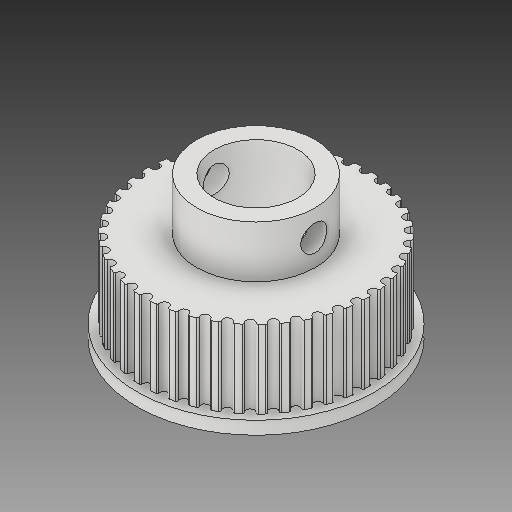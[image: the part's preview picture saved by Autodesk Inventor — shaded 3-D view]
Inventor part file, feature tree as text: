
AUTODESK INVENTOR PART (.ipt)
format: ipt  version: 2018.2 (Build 222227000, 227)  size: 381,952 bytes
history: native  units: mm
features: extrude x6, sketch x5, pattern_circular x1
ambient origin geometry x8: Origin, YZ Plane, XZ Plane, XY Plane, X Axis, Y Axis, Z Axis, Center Point
bodies: Solid1 (feature_tree)
feature tree (12):
  extrude  "Extrusion1"  Depth=0.5mm
  extrude  "Extrusion2"  Depth=7.0mm TaperAngle=0.0deg
  pattern_circular  "Circular Pattern1"  [2 undecoded]
  extrude  "Extrusion3"  Depth=1.0mm TaperAngle=0.0deg
  sketch  "Sketch4"  dims[d18=9.7mm]
  extrude  "Extrusion4"  Depth=6.0mm TaperAngle=0.0deg
  extrude  "Extrusion5"  Depth=3.0mm
  extrude  "Extrusion6"  Depth=6.0mm TaperAngle=0.0deg
  sketch  "Sketch1"  dims[d8=0.0mm d9=0.5mm]
  sketch  "Sketch2"  dims[d10=0.15mm d12=7.0mm d13=0.0mm]
  sketch  "Sketch3"  dims[d15=360.0deg]
  sketch  "Sketch5"  dims[d20=0.0mm d21=2.0mm d22=1.0mm d23=0.0mm d24=6.0mm d25=0.0mm d26=3.0mm d27=6.0mm d28=0.0mm]
note: 2 required parameter values undecoded (feature->parameter linkage not recoverable at this tier; creation-order binding heuristic only, values carry confidence <= 0.55)
